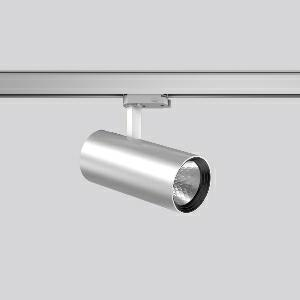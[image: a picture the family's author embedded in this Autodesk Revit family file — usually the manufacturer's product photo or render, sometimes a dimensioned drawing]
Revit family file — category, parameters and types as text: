
# Revit family: deecos_s_mini_742205_004_3_76_9a2a
name_source: partatom
category: Lighting Fixtures
units: mm (PartAtom-declared; Revit-internal decimal feet)

## family parameters
Cut with Voids When Loaded = No
Host = Face
Light Source = No
Part Type = Normal
Room Calculation Point = No
Round Connector Dimension = Use Diameter
Shared = No

## types (1)
- DEECOS S mini (1 x LED Modul 935, 3800 lm, 3500)
    Apparent Load = 29 VA
    Approval mark = CE
    CIE Flux Codes = 95 99 100 100 100
    Color Rendering = 92
    Color Temperature = 3500
    Default Elevation = 1800 mm
    Description = Series: DEECOS S mini
LED surface-mounted projector in modern design with no visible cooling ribs. Housing: die-cast aluminium, powder-coated. Rotation range: 356°. Swivel range: 90°. Black plastic ring and recessed LED to prevent glare from the side. Optical assembly with reflector made of MIRO-Silver with 98% total light reflection for outstanding efficiency - can be changed without tools. Best colour rendering index Ra>90. With adapter for RZB 3-circuit DALI tracks. Suitable for Track on ceiling, Wall track. High quality converter without flickering and stroboscopic effect. The following accessories can be mounted without use of tools: interchangeable lenses, decorative glasses, honeycomb louvre, clear and frosted diffusers, white interchangeable plastic ring. 
Colour: silver
Diameter: 87 mm
Height: 214 mm
Lamp: LED
Socket: without socket
Colour temperature: 3500K
Colour rendering index (CRI): 92
System power: 29 W
Rated luminous flux: 3800 lm
Luminous efficiency: 131 lm/W
Control gear: Converter, dimmable, DALI
Protection class: I
Type of protection: IP 20
    Height = 214 mm
    Lamp = 1 x LED Modul 935
    Lamp Light Flux = 3800 lm
    Lamp count = 1
    Length = 87 mm
    Lifetime = 50000 h
    Luminous efficacy = 131 lm/W
    Manufacturer = RZB
    ModVariant = No
    Model = 742205.004.3.76
    Mounting Place = Ceiling
    Mounting Type = Rail mounted
    Number of Poles = 1
    OnlyDefault = Yes
    Power Factor = 1
    Product Name = DEECOS S mini
    Product group = Track mounted projectors
    ProductGroupID = 301
    Protection Class = Protection class I
    Protection Degree = IP 20
    RLX_Detail_Level = 1
    RLX_Emergency_Light_Flux = 0 lm
    RLX_Emergency_Type = 0
    RLX_Emergency_Type_DB = No
    RlxData = <blob elided: 36789 chars, md5=fd0da4b7>
    Socket = socket
    Standby Power = 0 W
    System Light Flux = 3800 lm
    System Power = 29 W
    Type Comments = Product without accessories
    Type Image = 741926.004.jpg
    URL = http://relux.com
    VarID = ---
    Voltage = 230 V
    Voltage Range = 220-240 V
    Weight = 0.00 kg
    Width = 0 mm  [stored 0 ft]

note: [stored X ft] marks values corroborated as IEEE doubles in the binary element streams (Revit-internal decimal feet)

## geometry (parser evidence)
native form markers: Blend x4, Sweep x10
no freeform markers — native parametric forms only
